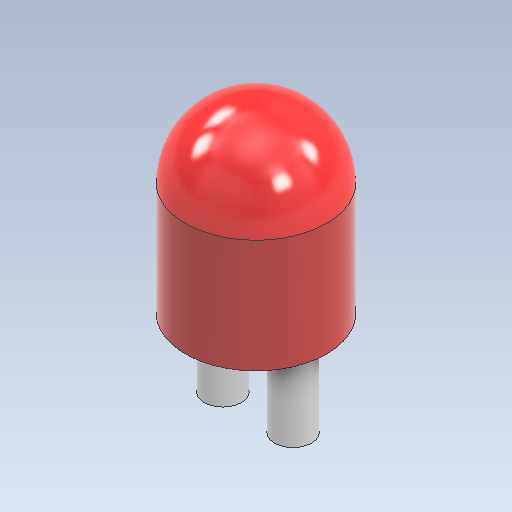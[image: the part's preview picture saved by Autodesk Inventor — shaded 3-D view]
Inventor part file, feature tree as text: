
AUTODESK INVENTOR PART (.ipt)
format: ipt  version: 2021 (Build 250183000, 183)  size: 140,800 bytes
history: native  units: mm
features: sketch x3, extrude x2, revolve x1
ambient origin geometry x8: Origin, YZ Plane, XZ Plane, XY Plane, X Axis, Y Axis, Z Axis, Center Point
bodies: Solid1 (feature_tree)
feature tree (6):
  revolve  "Revolution1"  Angle=180.0deg
  extrude  "Extrusion1"  Depth=30.0mm TaperAngle=0.0deg
  extrude  "Extrusion2"  [1 undecoded]
  sketch  "Sketch1"  dims[d0=50.0mm d1=180.0deg]
  sketch  "Sketch2"  dims[d2=40.0mm d3=0.0mm d4=30.0mm d5=0.0mm]
  sketch  "Sketch3"
note: 1 required parameter value undecoded (feature->parameter linkage not recoverable at this tier; creation-order binding heuristic only, values carry confidence <= 0.55)
